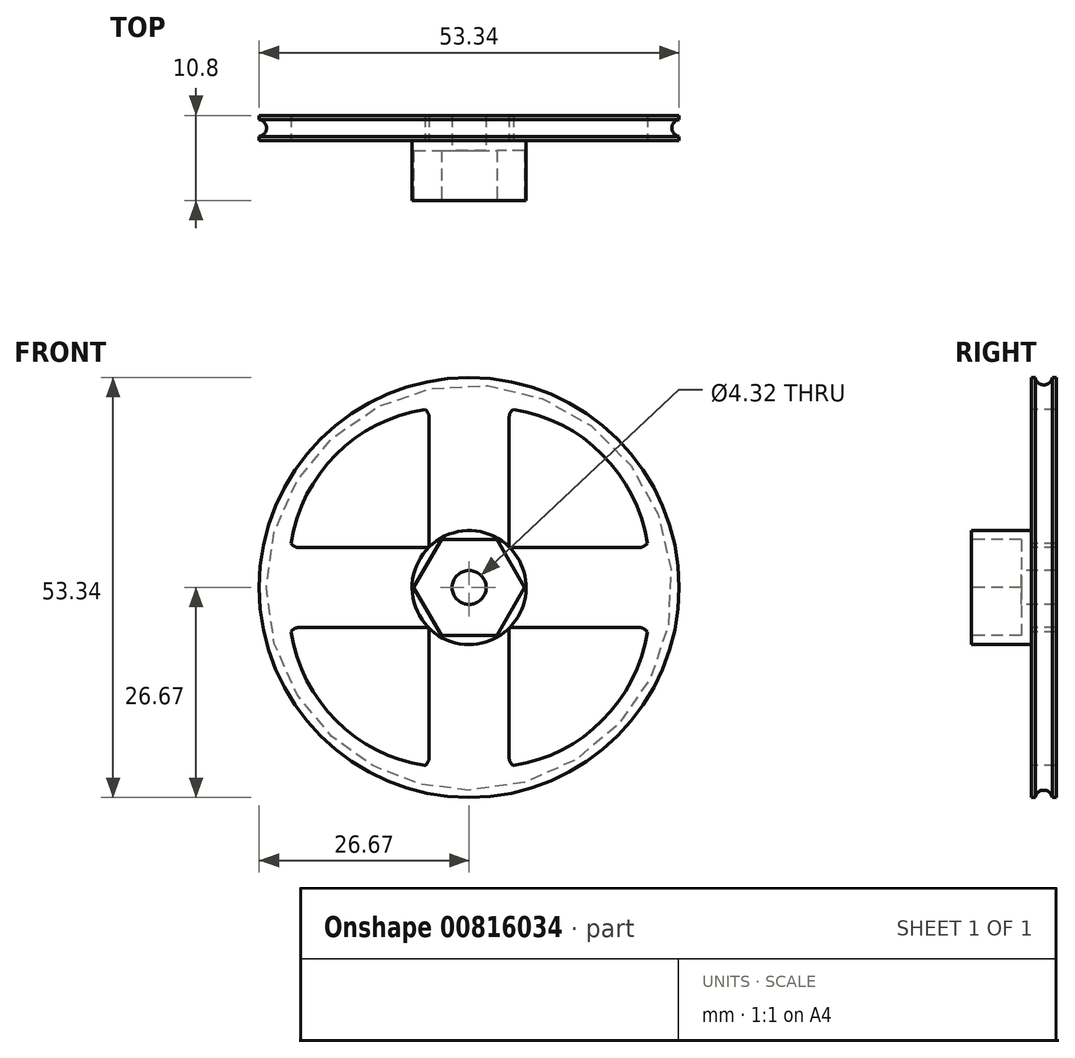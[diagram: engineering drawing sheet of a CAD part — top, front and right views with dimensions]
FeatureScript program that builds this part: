
annotation { "Feature Type Name" : "Feature", "Feature Type Description" : "" }
export const myFeature = defineFeature(function(context is Context, id is Id, definition is map)
    precondition{}
    {
        {
            var Q0;
            Q0=qCreatedBy(makeId("Front.planeOp"),FACE);
            var sketch = newSketch(context, id + "F0", { "sketchPlane" : qUnion([Q0])});
            skCircle(sketch, "E0", {"center": v(0, 0) * mm, "radius": 26.67 * mm});
            skSolve(sketch);
        }
        {
            var Q0;
            Q0 = qSketchRegion(id + "F0", true);
            extrude(context, id + "F1", {"entities" : qUnion([Q0]), "depth" : 3.17 * mm, "offsetDistance" : 25.4 * mm});
        }
        {
            var Q0;
            Q0=makeQuery(id+"F1.opExtrude","CAP_FACE",FACE,{"disambiguationData":[OSD([sQuery(id+"F0.wireOp",EDGE,"E0")])],"isStart":false});
            var sketch = newSketch(context, id + "F2", { "sketchPlane" : qUnion([Q0])});
            skLineSegment(sketch, "E1", {"start": v(0, 0) * mm, "end": v(0, -26.67) * mm, "construction": true});
            skLineSegment(sketch, "E2", {"start": v(0, 0) * mm, "end": v(0, 26.67) * mm, "construction": true});
            skLineSegment(sketch, "E3", {"start": v(0, 0) * mm, "end": v(26.67, 0) * mm, "construction": true});
            skLineSegment(sketch, "E4", {"start": v(0, 0) * mm, "end": v(-26.67, 0) * mm, "construction": true});
            skLineSegment(sketch, "E5", {"start": v(0, 0) * mm, "end": v(0, 5.08) * mm});
            skLineSegment(sketch, "E6", {"start": v(0, 0) * mm, "end": v(-5.08, 0) * mm, "construction": true});
            skLineSegment(sketch, "E7", {"start": v(-5.08, 0) * mm, "end": v(-5.08, 5.08) * mm, "construction": true});
            skLineSegment(sketch, "E8", {"start": v(-5.08, 5.08) * mm, "end": v(0, 5.08) * mm, "construction": true});
            skLineSegment(sketch, "E9.bottom", {"start": v(-5.08, 5.08) * mm, "end": v(-21.59, 5.08) * mm});
            skLineSegment(sketch, "E9.left", {"start": v(-5.08, 5.08) * mm, "end": v(-5.08, 21.59) * mm});
            skPoint(sketch, "E10.visualSharp", {"position": v(-22.86, 5.08) * mm});
            skPoint(sketch, "E11.visualSharp", {"position": v(-5.08, 22.86) * mm});
            skPoint(sketch, "E12.visualSharp", {"position": v(-22.86, 22.86) * mm});
            skArc(sketch, "E12.filletArc", {"start": v(-5.62, 22.63) * mm, "mid": v(-16.9, 16.9) * mm, "end": v(-22.63, 5.62) * mm});
            skArc(sketch, "E13", {"start": v(-22.63, 5.62) * mm, "mid": v(-22.17, 5.22) * mm, "end": v(-21.59, 5.08) * mm});
            skArc(sketch, "E14", {"start": v(-5.08, 21.59) * mm, "mid": v(-5.22, 22.17) * mm, "end": v(-5.62, 22.63) * mm});
            skArc(sketch, "E15.1.0", {"start": v(-22.63, -5.62) * mm, "mid": v(-16.9, -16.9) * mm, "end": v(-5.62, -22.63) * mm});
            skLineSegment(sketch, "E15.1.1", {"start": v(-5.08, -5.08) * mm, "end": v(-21.59, -5.08) * mm});
            skLineSegment(sketch, "E15.1.2", {"start": v(-5.08, -5.08) * mm, "end": v(-5.08, -21.59) * mm});
            skPoint(sketch, "E15.1.3", {"position": v(-5.08, -22.86) * mm});
            skPoint(sketch, "E15.1.4", {"position": v(-22.86, -5.08) * mm});
            skPoint(sketch, "E15.1.5", {"position": v(-22.86, -22.86) * mm});
            skArc(sketch, "E15.1.6", {"start": v(-21.59, -5.08) * mm, "mid": v(-22.17, -5.22) * mm, "end": v(-22.63, -5.62) * mm});
            skArc(sketch, "E15.1.7", {"start": v(-5.62, -22.63) * mm, "mid": v(-5.22, -22.17) * mm, "end": v(-5.08, -21.59) * mm});
            skArc(sketch, "E15.2.0", {"start": v(5.62, -22.63) * mm, "mid": v(16.9, -16.9) * mm, "end": v(22.63, -5.62) * mm});
            skLineSegment(sketch, "E15.2.1", {"start": v(5.08, -5.08) * mm, "end": v(5.08, -21.59) * mm});
            skLineSegment(sketch, "E15.2.2", {"start": v(5.08, -5.08) * mm, "end": v(21.59, -5.08) * mm});
            skPoint(sketch, "E15.2.3", {"position": v(22.86, -5.08) * mm});
            skPoint(sketch, "E15.2.4", {"position": v(5.08, -22.86) * mm});
            skPoint(sketch, "E15.2.5", {"position": v(22.86, -22.86) * mm});
            skArc(sketch, "E15.2.6", {"start": v(5.08, -21.59) * mm, "mid": v(5.22, -22.17) * mm, "end": v(5.62, -22.63) * mm});
            skArc(sketch, "E15.2.7", {"start": v(22.63, -5.62) * mm, "mid": v(22.17, -5.22) * mm, "end": v(21.59, -5.08) * mm});
            skArc(sketch, "E15.3.0", {"start": v(22.63, 5.62) * mm, "mid": v(16.9, 16.9) * mm, "end": v(5.62, 22.63) * mm});
            skLineSegment(sketch, "E15.3.1", {"start": v(5.08, 5.08) * mm, "end": v(21.6, 5.08) * mm});
            skLineSegment(sketch, "E15.3.2", {"start": v(5.08, 5.08) * mm, "end": v(5.08, 21.59) * mm});
            skPoint(sketch, "E15.3.3", {"position": v(5.08, 22.86) * mm});
            skPoint(sketch, "E15.3.4", {"position": v(22.86, 5.08) * mm});
            skPoint(sketch, "E15.3.5", {"position": v(22.86, 22.86) * mm});
            skArc(sketch, "E15.3.6", {"start": v(21.59, 5.08) * mm, "mid": v(22.17, 5.22) * mm, "end": v(22.63, 5.62) * mm});
            skArc(sketch, "E15.3.7", {"start": v(5.62, 22.63) * mm, "mid": v(5.22, 22.17) * mm, "end": v(5.08, 21.59) * mm});
            skPoint(sketch, "E15.center", {"position": v(0, 0) * mm});
            skSolve(sketch);
        }
        {
            var Q0;
            Q0 = qSketchRegion(id + "F2", true);
            extrude(context, id + "F3", {"entities" : qUnion([Q0]), "operationType" : NewBodyOperationType.REMOVE, "oppositeDirection" : true, "depth" : 25.4 * mm, "offsetDistance" : 25.4 * mm});
        }
        {
            var Q0;
            Q0=makeQuery(id+"F1.opExtrude","CAP_FACE",FACE,{"disambiguationData":[OSD([sQuery(id+"F0.wireOp",EDGE,"E0")])],"isStart":false});
            var sketch = newSketch(context, id + "F4", { "sketchPlane" : qUnion([Q0])});
            skCircle(sketch, "E16", {"center": v(0, 0) * mm, "radius": 7.24 * mm});
            skSolve(sketch);
        }
        {
            var Q0;
            Q0 = qSketchRegion(id + "F4", true);
            extrude(context, id + "F5", {"entities" : qUnion([Q0]), "operationType" : NewBodyOperationType.ADD, "depth" : 7.62 * mm, "offsetDistance" : 25.4 * mm});
        }
        {
            var Q0;
            Q0=makeQuery(id+"F5.opExtrude","CAP_FACE",FACE,{"disambiguationData":[OSD([sQuery(id+"F4.wireOp",EDGE,"E16")])],"isStart":false});
            var sketch = newSketch(context, id + "F6", { "sketchPlane" : qUnion([Q0])});
            skCircle(sketch, "E17.cCircle", {"center": v(0, 0) * mm, "radius": 7.04 * mm, "construction": true});
            skLineSegment(sketch, "E17.0", {"start": v(7.04, 0) * mm, "end": v(3.52, -6.1) * mm});
            skLineSegment(sketch, "E17.1", {"start": v(3.52, -6.1) * mm, "end": v(-3.52, -6.1) * mm});
            skLineSegment(sketch, "E17.2", {"start": v(-3.52, -6.1) * mm, "end": v(-7.04, 0) * mm});
            skLineSegment(sketch, "E17.3", {"start": v(-7.04, 0) * mm, "end": v(-3.52, 6.1) * mm});
            skLineSegment(sketch, "E17.4", {"start": v(-3.52, 6.1) * mm, "end": v(3.52, 6.1) * mm});
            skLineSegment(sketch, "E17.5", {"start": v(3.52, 6.1) * mm, "end": v(7.04, 0) * mm});
            skSolve(sketch);
        }
        {
            var Q0;
            Q0 = qSketchRegion(id + "F6", true);
            extrude(context, id + "F7", {"entities" : qUnion([Q0]), "operationType" : NewBodyOperationType.REMOVE, "oppositeDirection" : true, "depth" : 6.35 * mm, "offsetDistance" : 25.4 * mm});
        }
        {
            var Q0;
            Q0=makeQuery(id+"F7.boolean.opBoolean","COPY",FACE,{"derivedFrom":makeQuery(id+"F7.opExtrude","CAP_FACE",FACE,{"disambiguationData":[OSD([sQuery(id+"F6.wireOp",EDGE,"E17.0"),sQuery(id+"F6.wireOp",EDGE,"E17.1"),sQuery(id+"F6.wireOp",EDGE,"E17.2"),sQuery(id+"F6.wireOp",EDGE,"E17.3"),sQuery(id+"F6.wireOp",EDGE,"E17.4"),sQuery(id+"F6.wireOp",EDGE,"E17.5")])],"isStart":false})});
            var sketch = newSketch(context, id + "F8", { "sketchPlane" : qUnion([Q0])});
            skCircle(sketch, "E18", {"center": v(0, 0) * mm, "radius": 2.16 * mm});
            skSolve(sketch);
        }
        {
            var Q0;
            Q0 = qSketchRegion(id + "F8", true);
            extrude(context, id + "F9", {"entities" : qUnion([Q0]), "operationType" : NewBodyOperationType.REMOVE, "oppositeDirection" : true, "depth" : 25.4 * mm, "offsetDistance" : 25.4 * mm});
        }
        {
            var Q0;
            Q0=qCreatedBy(makeId("Top.planeOp"),FACE);
            var sketch = newSketch(context, id + "F10", { "sketchPlane" : qUnion([Q0])});
            skLineSegment(sketch, "E19", {"start": v(0, 0) * mm, "end": v(0, -3.18) * mm, "construction": true});
            skLineSegment(sketch, "E20", {"start": v(0, -3.18) * mm, "end": v(26.67, -3.18) * mm, "construction": true});
            skLineSegment(sketch, "E21", {"start": v(26.67, -3.17) * mm, "end": v(26.67, 0) * mm, "construction": true});
            skLineSegment(sketch, "E22", {"start": v(26.67, 0) * mm, "end": v(0, 0) * mm, "construction": true});
            skLineSegment(sketch, "E23", {"start": v(26.67, -3.18) * mm, "end": v(26.67, -2.67) * mm});
            skLineSegment(sketch, "E24", {"start": v(26.67, 0) * mm, "end": v(26.67, -0.5) * mm});
            skArc(sketch, "E25", {"start": v(26.67, -0.5) * mm, "mid": v(25.74, -1.59) * mm, "end": v(26.67, -2.67) * mm});
            skLineSegment(sketch, "E26", {"start": v(26.67, -2.67) * mm, "end": v(26.67, -0.5) * mm});
            skSolve(sketch);
        }
        {
            var Q0;
            Q0 = qSketchRegion(id + "F10", true);
            var Q1;
            Q1=sQuery(id+"F10.wireOp",EDGE,"E19");
            revolve(context, id + "F11", {"operationType" : NewBodyOperationType.REMOVE, "surfaceOperationType" : NewSurfaceOperationType.NEW, "entities" : qUnion([Q0]), "axis" : qUnion([Q1]), "revolveType" : RevolveType.FULL, "oppositeDirection" : true});
        }
    });
